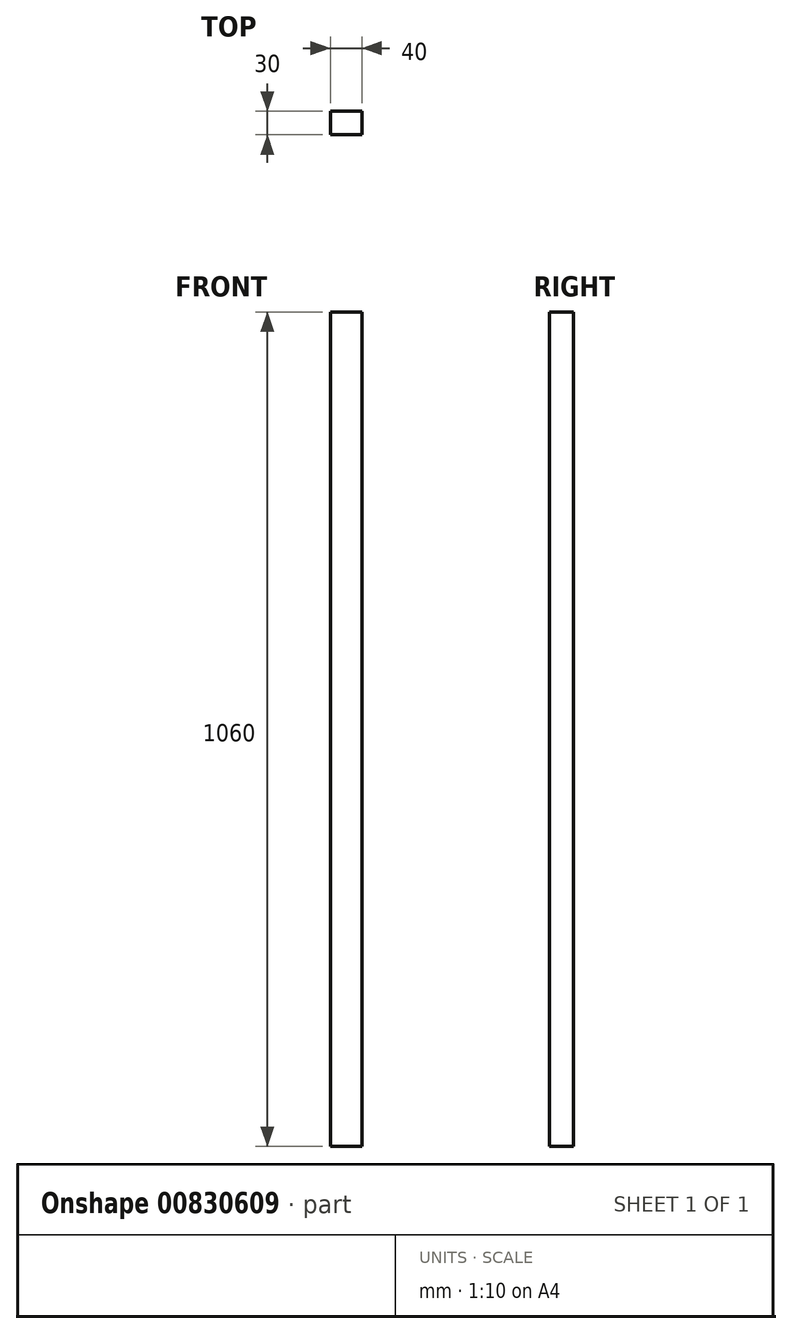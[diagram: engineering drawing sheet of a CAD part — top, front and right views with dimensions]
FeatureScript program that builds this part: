
annotation { "Feature Type Name" : "Feature", "Feature Type Description" : "" }
export const myFeature = defineFeature(function(context is Context, id is Id, definition is map)
    precondition{}
    {
        {
            var Q0;
            Q0=qCreatedBy(makeId("Top.planeOp"),FACE);
            var sketch = newSketch(context, id + "F0", { "sketchPlane" : qUnion([Q0])});
            skLineSegment(sketch, "E0.bottom", {"start": v(3.01, 0) * mm, "end": v(43.01, 0) * mm});
            skLineSegment(sketch, "E0.top", {"start": v(3.01, 30) * mm, "end": v(43.01, 30) * mm});
            skLineSegment(sketch, "E0.left", {"start": v(3.01, 0) * mm, "end": v(3.01, 30) * mm});
            skLineSegment(sketch, "E0.right", {"start": v(43.01, 0) * mm, "end": v(43.01, 30) * mm});
            skSolve(sketch);
        }
        {
            var Q0;
            Q0=makeQuery(id+"F0.imprint","IMPRINT",FACE,{"disambiguationData":[TD([[makeQuery(id+"F0.imprint","IMPRINT",EDGE,{"derivedFrom":sQuery(id+"F0.wireOp",EDGE,"E0.bottom")}),1.0]])]});
            extrude(context, id + "F1", {"entities" : qUnion([Q0]), "depth" : 1060 * mm, "offsetDistance" : 25 * mm});
        }
    });
